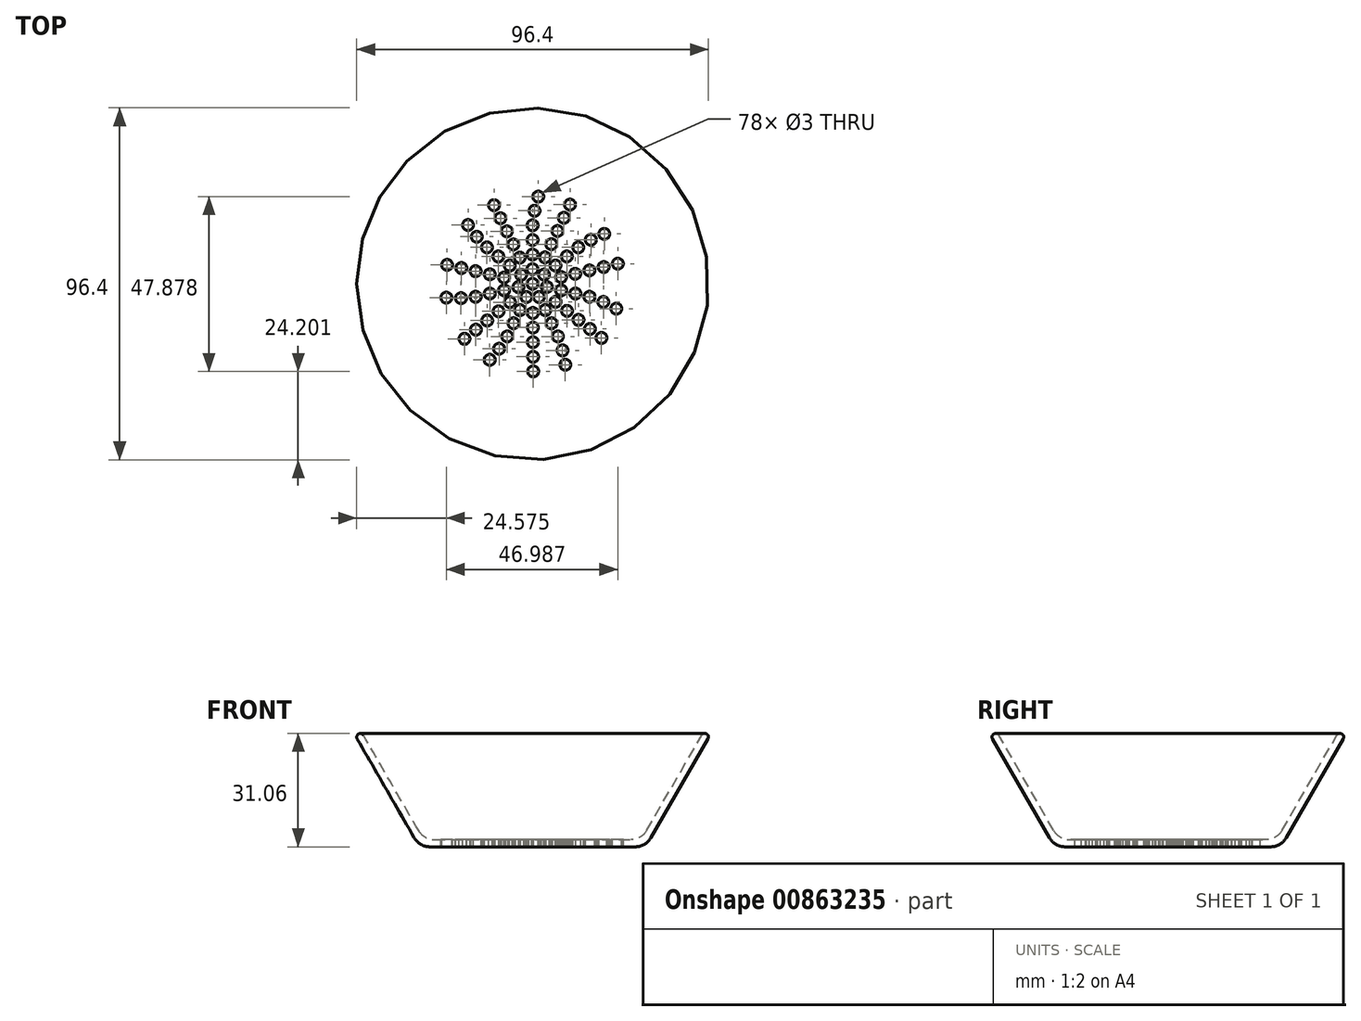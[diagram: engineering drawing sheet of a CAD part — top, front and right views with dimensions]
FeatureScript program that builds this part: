
annotation { "Feature Type Name" : "Feature", "Feature Type Description" : "" }
export const myFeature = defineFeature(function(context is Context, id is Id, definition is map)
    precondition{}
    {
        {
            var Q0;
            Q0=qCreatedBy(makeId("Front.planeOp"),FACE);
            var sketch = newSketch(context, id + "F0", { "sketchPlane" : qUnion([Q0])});
            skLineSegment(sketch, "E0", {"start": v(0, 0) * mm, "end": v(26.96, 0) * mm});
            skLineSegment(sketch, "E1", {"start": v(31.29, 2.5) * mm, "end": v(46.33, 28.56) * mm});
            skLineSegment(sketch, "E2.0", {"start": v(32.44, 0.5) * mm, "end": v(48.06, 27.56) * mm});
            skLineSegment(sketch, "E2.1", {"start": v(0, -2) * mm, "end": v(28.11, -2) * mm});
            skLineSegment(sketch, "E3", {"start": v(47.81, 28.85) * mm, "end": v(47.81, 28.85) * mm});
            skLineSegment(sketch, "E4", {"start": v(0, -2) * mm, "end": v(0, 47.87) * mm});
            skPoint(sketch, "E5.visualSharp", {"position": v(31, -2) * mm});
            skArc(sketch, "E5.filletArc", {"start": v(28.11, -2) * mm, "mid": v(30.61, -1.33) * mm, "end": v(32.44, 0.5) * mm});
            skPoint(sketch, "E6.visualSharp", {"position": v(29.85, 0) * mm});
            skArc(sketch, "E6.filletArc", {"start": v(26.96, 0) * mm, "mid": v(29.46, 0.67) * mm, "end": v(31.29, 2.5) * mm});
            skPoint(sketch, "E7.visualSharp", {"position": v(48.5, 28.31) * mm});
            skArc(sketch, "E7.filletArc", {"start": v(48.06, 27.56) * mm, "mid": v(48.18, 28.25) * mm, "end": v(47.81, 28.85) * mm});
            skPoint(sketch, "E8.visualSharp", {"position": v(46.9, 29.55) * mm});
            skArc(sketch, "E8.filletArc", {"start": v(47.81, 28.85) * mm, "mid": v(47, 29.04) * mm, "end": v(46.33, 28.56) * mm});
            skSolve(sketch);
        }
        {
            var Q0;
            Q0=qSketchRegion(id+"F0",true);
            var Q1;
            Q1=sQuery(id+"F0.wireOp",EDGE,"E4");
            revolve(context, id + "F1", {"surfaceOperationType" : NewSurfaceOperationType.NEW, "entities" : qUnion([Q0]), "axis" : qUnion([Q1]), "revolveType" : RevolveType.FULL});
        }
        {
            var Q0;
            Q0=makeQuery(id+"F1.opRevolve","SWEPT_FACE",FACE,{"disambiguationData":[OSD([sQuery(id+"F0.wireOp",EDGE,"E0")])]});
            var sketch = newSketch(context, id + "F2", { "sketchPlane" : qUnion([Q0])});
            skCircle(sketch, "E9", {"center": v(0.54, 20.01) * mm, "radius": 1.5 * mm});
            skCircle(sketch, "E10", {"center": v(0, 16.01) * mm, "radius": 1.5 * mm});
            skCircle(sketch, "E11", {"center": v(0, 12.01) * mm, "radius": 1.5 * mm});
            skCircle(sketch, "E12", {"center": v(0, 8.01) * mm, "radius": 1.5 * mm});
            skCircle(sketch, "E13", {"center": v(-0.02, 4.01) * mm, "radius": 1.5 * mm});
            skCircle(sketch, "E14", {"center": v(1.55, 23.88) * mm, "radius": 1.5 * mm});
            skCircle(sketch, "E15.1.0", {"center": v(-3.15, 2.48) * mm, "radius": 1.5 * mm});
            skCircle(sketch, "E15.1.1", {"center": v(-9.39, 7.49) * mm, "radius": 1.5 * mm});
            skCircle(sketch, "E15.1.2", {"center": v(-6.26, 5) * mm, "radius": 1.5 * mm});
            skCircle(sketch, "E15.1.3", {"center": v(-12.52, 9.98) * mm, "radius": 1.5 * mm});
            skCircle(sketch, "E15.1.4", {"center": v(-15.31, 12.9) * mm, "radius": 1.5 * mm});
            skCircle(sketch, "E15.1.5", {"center": v(-17.7, 16.1) * mm, "radius": 1.5 * mm});
            skCircle(sketch, "E15.2.0", {"center": v(-3.9, -0.91) * mm, "radius": 1.5 * mm});
            skCircle(sketch, "E15.2.1", {"center": v(-11.7, -2.67) * mm, "radius": 1.5 * mm});
            skCircle(sketch, "E15.2.2", {"center": v(-7.8, -1.78) * mm, "radius": 1.5 * mm});
            skCircle(sketch, "E15.2.3", {"center": v(-15.6, -3.56) * mm, "radius": 1.5 * mm});
            skCircle(sketch, "E15.2.4", {"center": v(-19.63, -3.93) * mm, "radius": 1.5 * mm});
            skCircle(sketch, "E15.2.5", {"center": v(-23.63, -3.8) * mm, "radius": 1.5 * mm});
            skPoint(sketch, "E15.center", {"position": v(0, 0) * mm});
            skCircle(sketch, "E16.1.3.0", {"center": v(-1.72, -3.62) * mm, "radius": 1.5 * mm});
            skCircle(sketch, "E16.2.3.0", {"center": v(-5.21, -10.82) * mm, "radius": 1.5 * mm});
            skCircle(sketch, "E16.4.3.0", {"center": v(-3.48, -7.22) * mm, "radius": 1.5 * mm});
            skCircle(sketch, "E16.6.3.0", {"center": v(-6.95, -14.42) * mm, "radius": 1.5 * mm});
            skCircle(sketch, "E16.8.3.0", {"center": v(-9.16, -17.8) * mm, "radius": 1.5 * mm});
            skCircle(sketch, "E16.10.3.0", {"center": v(-11.76, -20.84) * mm, "radius": 1.5 * mm});
            skCircle(sketch, "E16.1.4.0", {"center": v(1.76, -3.6) * mm, "radius": 1.5 * mm});
            skCircle(sketch, "E16.2.4.0", {"center": v(5.21, -10.82) * mm, "radius": 1.5 * mm});
            skCircle(sketch, "E16.4.4.0", {"center": v(3.48, -7.22) * mm, "radius": 1.5 * mm});
            skCircle(sketch, "E16.6.4.0", {"center": v(6.95, -14.42) * mm, "radius": 1.5 * mm});
            skCircle(sketch, "E16.8.4.0", {"center": v(8.2, -18.26) * mm, "radius": 1.5 * mm});
            skCircle(sketch, "E16.10.4.0", {"center": v(8.96, -22.19) * mm, "radius": 1.5 * mm});
            skCircle(sketch, "E16.1.5.0", {"center": v(3.91, -0.87) * mm, "radius": 1.5 * mm});
            skCircle(sketch, "E16.2.5.0", {"center": v(11.7, -2.67) * mm, "radius": 1.5 * mm});
            skCircle(sketch, "E16.4.5.0", {"center": v(7.8, -1.78) * mm, "radius": 1.5 * mm});
            skCircle(sketch, "E16.6.5.0", {"center": v(15.6, -3.56) * mm, "radius": 1.5 * mm});
            skCircle(sketch, "E16.8.5.0", {"center": v(19.39, -4.97) * mm, "radius": 1.5 * mm});
            skCircle(sketch, "E16.10.5.0", {"center": v(22.93, -6.83) * mm, "radius": 1.5 * mm});
            skCircle(sketch, "E16.1.6.0", {"center": v(3.12, 2.52) * mm, "radius": 1.5 * mm});
            skCircle(sketch, "E16.2.6.0", {"center": v(9.39, 7.49) * mm, "radius": 1.5 * mm});
            skCircle(sketch, "E16.4.6.0", {"center": v(6.26, 5) * mm, "radius": 1.5 * mm});
            skCircle(sketch, "E16.6.6.0", {"center": v(12.52, 9.98) * mm, "radius": 1.5 * mm});
            skCircle(sketch, "E16.8.6.0", {"center": v(15.98, 12.06) * mm, "radius": 1.5 * mm});
            skCircle(sketch, "E16.10.6.0", {"center": v(19.64, 13.67) * mm, "radius": 1.5 * mm});
            skLineSegment(sketch, "E17", {"start": v(0, 0) * mm, "end": v(-20.96, -16.95) * mm});
            skLineSegment(sketch, "E18", {"start": v(-23.63, -3.8) * mm, "end": v(-11.76, -20.84) * mm});
            skCircle(sketch, "E19", {"center": v(-18.66, -15.09) * mm, "radius": 1.5 * mm});
            skCircle(sketch, "E20", {"center": v(-15.55, -12.57) * mm, "radius": 1.5 * mm});
            skCircle(sketch, "E21", {"center": v(-12.44, -10.06) * mm, "radius": 1.5 * mm});
            skCircle(sketch, "E22", {"center": v(-9.33, -7.54) * mm, "radius": 1.5 * mm});
            skCircle(sketch, "E23", {"center": v(-6.22, -5.03) * mm, "radius": 1.5 * mm});
            skCircle(sketch, "E24.1.0", {"center": v(0.05, -8) * mm, "radius": 1.5 * mm});
            skCircle(sketch, "E24.1.1", {"center": v(0.08, -12) * mm, "radius": 1.5 * mm});
            skCircle(sketch, "E24.1.2", {"center": v(0.1, -16) * mm, "radius": 1.5 * mm});
            skCircle(sketch, "E24.1.3", {"center": v(0.13, -20) * mm, "radius": 1.5 * mm});
            skCircle(sketch, "E24.1.4", {"center": v(0.16, -24) * mm, "radius": 1.5 * mm});
            skCircle(sketch, "E24.2.0", {"center": v(6.29, -4.95) * mm, "radius": 1.5 * mm});
            skCircle(sketch, "E24.2.1", {"center": v(9.43, -7.42) * mm, "radius": 1.5 * mm});
            skCircle(sketch, "E24.2.2", {"center": v(12.58, -9.9) * mm, "radius": 1.5 * mm});
            skCircle(sketch, "E24.2.3", {"center": v(15.72, -12.36) * mm, "radius": 1.5 * mm});
            skCircle(sketch, "E24.2.4", {"center": v(18.86, -14.84) * mm, "radius": 1.5 * mm});
            skCircle(sketch, "E24.3.0", {"center": v(7.79, 1.83) * mm, "radius": 1.5 * mm});
            skCircle(sketch, "E24.3.1", {"center": v(11.68, 2.75) * mm, "radius": 1.5 * mm});
            skCircle(sketch, "E24.3.2", {"center": v(15.57, 3.67) * mm, "radius": 1.5 * mm});
            skCircle(sketch, "E24.3.3", {"center": v(19.47, 4.58) * mm, "radius": 1.5 * mm});
            skCircle(sketch, "E24.3.4", {"center": v(23.36, 5.5) * mm, "radius": 1.5 * mm});
            skCircle(sketch, "E24.4.0", {"center": v(3.42, 7.23) * mm, "radius": 1.5 * mm});
            skCircle(sketch, "E24.4.1", {"center": v(5.13, 10.85) * mm, "radius": 1.5 * mm});
            skCircle(sketch, "E24.4.2", {"center": v(6.84, 14.46) * mm, "radius": 1.5 * mm});
            skCircle(sketch, "E24.4.3", {"center": v(8.56, 18.08) * mm, "radius": 1.5 * mm});
            skCircle(sketch, "E24.4.4", {"center": v(10.27, 21.7) * mm, "radius": 1.5 * mm});
            skCircle(sketch, "E24.5.0", {"center": v(-3.52, 7.18) * mm, "radius": 1.5 * mm});
            skCircle(sketch, "E24.5.1", {"center": v(-5.28, 10.78) * mm, "radius": 1.5 * mm});
            skCircle(sketch, "E24.5.2", {"center": v(-7.04, 14.37) * mm, "radius": 1.5 * mm});
            skCircle(sketch, "E24.5.3", {"center": v(-8.8, 17.96) * mm, "radius": 1.5 * mm});
            skCircle(sketch, "E24.5.4", {"center": v(-10.56, 21.55) * mm, "radius": 1.5 * mm});
            skCircle(sketch, "E24.6.0", {"center": v(-7.81, 1.73) * mm, "radius": 1.5 * mm});
            skCircle(sketch, "E24.6.1", {"center": v(-11.72, 2.6) * mm, "radius": 1.5 * mm});
            skCircle(sketch, "E24.6.2", {"center": v(-15.62, 3.46) * mm, "radius": 1.5 * mm});
            skCircle(sketch, "E24.6.3", {"center": v(-19.53, 4.32) * mm, "radius": 1.5 * mm});
            skCircle(sketch, "E24.6.4", {"center": v(-23.43, 5.18) * mm, "radius": 1.5 * mm});
            skCircle(sketch, "E25", {"center": v(0, 0) * mm, "radius": 1.5 * mm});
            skSolve(sketch);
        }
        {
            var Q0;
            Q0=qSketchRegion(id+"F2",true);
            extrude(context, id + "F3", {"entities" : qUnion([Q0]), "operationType" : NewBodyOperationType.REMOVE, "oppositeDirection" : true, "depth" : 25 * mm, "offsetDistance" : 25 * mm});
        }
    });
